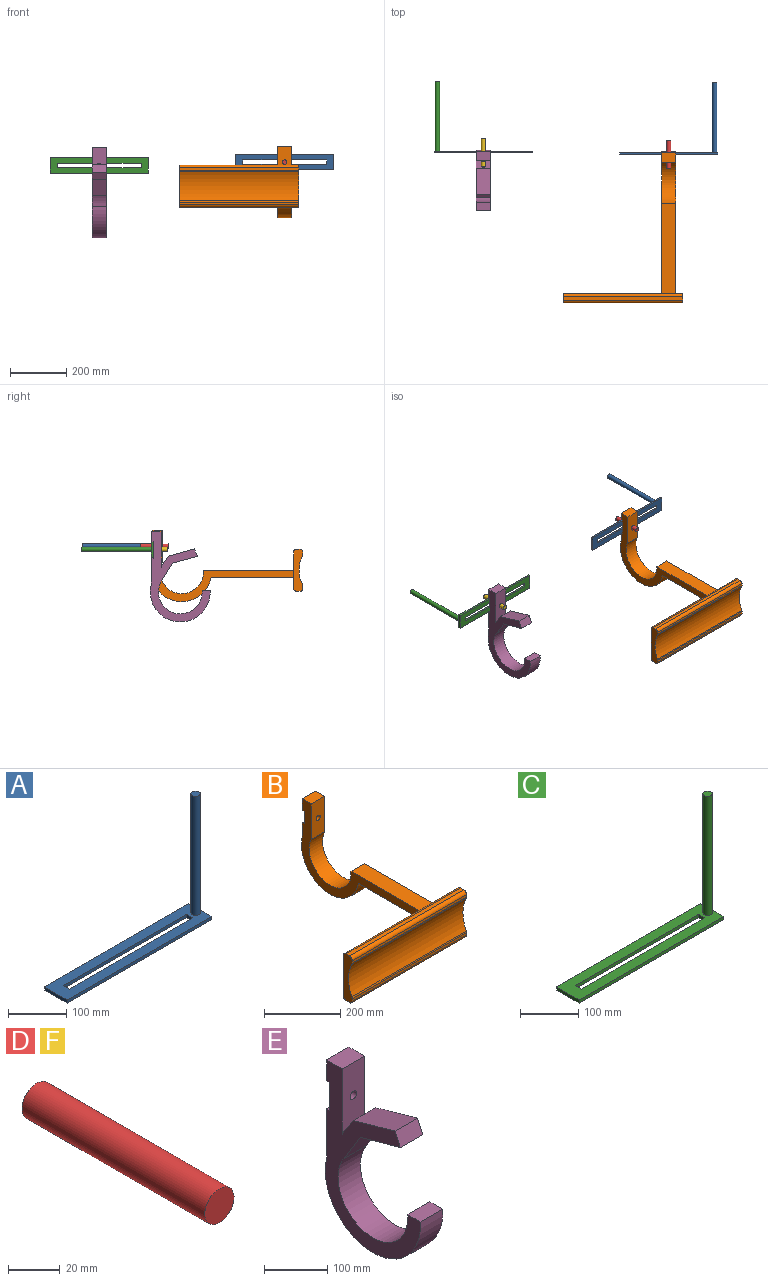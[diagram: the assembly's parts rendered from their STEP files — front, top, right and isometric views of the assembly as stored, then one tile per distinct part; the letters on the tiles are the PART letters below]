
ASSEMBLY  parts=6 mates=4
PART A: 12 faces, bbox 350x54.6x256.5 mm
  f0: plane 350x54.58mm, normal (0,0,1), area 14418.2mm2, adj f1,f3,f4,f5,f6,f7,f8,f9
  f1: plane 350x6.45mm, normal (0,-1,0), area 2257.7mm2, adj f0,f2,f4,f5
  f2: plane 350x54.58mm, normal (0,0,-1), area 14619.2mm2, adj f1,f3,f4,f5,f6,f7,f8,f9
  f3: plane 350x6.45mm, normal (0,1,0), area 2257.7mm2, adj f0,f2,f4,f5
  f4: plane 54.58x6.45mm, normal (1,0,0), area 352.1mm2, adj f0,f1,f2,f3
  f5: plane 54.58x6.45mm, normal (-1,0,0), area 352.1mm2, adj f0,f1,f2,f3
  f6: plane 15x6.45mm, normal (1,0,0), area 96.8mm2, adj f0,f2,f7,f9
  f7: plane 298.97x6.45mm, normal (0,1,0), area 1928.6mm2, adj f0,f2,f6,f8
  f8: plane 15x6.45mm, normal (-1,0,0), area 96.8mm2, adj f0,f2,f7,f9
  f9: plane 298.97x6.45mm, normal (0,-1,0), area 1928.6mm2, adj f0,f2,f6,f8
  f10: cylinder r=8mm len=250mm, axis (0,0,-1), area 12566.4mm2, adj f0,f11
  f11: plane 16x16mm, normal (0,0,1), area 201.1mm2, adj f10
PART B: 31 faces, bbox 425x538.8x255.6 mm
  f0: plane 50x41.78mm, normal (0,1,0), area 2089.1mm2, adj f1,f2,f7,f29
  f1: plane 505.7x255.65mm, normal (-1,0,0), area 20440.9mm2, adj f0,f5,f6,f7,f8,f9,f10,f11
  f2: plane 505.7x255.65mm, normal (1,0,0), area 20440.9mm2, adj f0,f5,f6,f7,f8,f9,f10,f11
  f3: cylinder r=7.5mm len=27.51mm, axis (0,-1,0), area 1296.5mm2, adj f26,f30
  f4: plane 425x7.79mm, normal (0,-1,0), area 3309mm2, adj f13,f16,f19,f22
  f5: plane 294.09x50mm, normal (0,0,-1), area 14704.4mm2, adj f1,f2,f7,f11
  f6: plane 321.33x50mm, normal (0,0,1), area 16066.6mm2, adj f1,f2,f9,f11
  f7: cylinder r=106.68mm len=211.61mm, axis (-1,0,0), area 17291.3mm2, adj f0,f1,f2,f5
  f8: cylinder r=77.9mm len=155.59mm, axis (-1,0,0), area 13733.1mm2, adj f1,f2,f9,f10
  f9: plane 50x11.5mm, normal (0,1,0), area 574.8mm2, adj f1,f2,f6,f8
  f10: plane 50x0.16mm, normal (0,-0.55,0.83), area 9.4mm2, adj f1,f2,f8,f25
  f11: plane 425x130mm, normal (0,1,0), area 54000mm2, adj f1,f2,f5,f6,f13,f16,f21,f23
  f12: plane 425x7.79mm, normal (0,-1,0), area 3309mm2, adj f13,f16,f18,f20
  f13: plane 150x33.08mm, normal (-1,0,0), area 3853.4mm2, adj f4,f11,f12,f14,f15,f17,f18,f19
  f14: plane 425x13.08mm, normal (0,0,1), area 5558.4mm2, adj f13,f16,f22,f23
  f15: plane 425x13.08mm, normal (0,0,-1), area 5558.4mm2, adj f13,f16,f20,f21
  f16: plane 150x33.08mm, normal (1,0,0), area 3853.4mm2, adj f4,f11,f12,f14,f15,f17,f18,f19
  f17: cylinder r=115.34mm len=425mm, axis (1,0,0), area 46473mm2, adj f13,f16,f18,f19
  f18: cylinder r=10mm len=425mm, axis (1,0,0), area 2014.7mm2, adj f12,f13,f16,f17
  f19: cylinder r=10mm len=425mm, axis (1,0,0), area 2014.7mm2, adj f4,f13,f16,f17
  f20: cylinder r=10mm len=425mm, axis (-1,0,0), area 6675.9mm2, adj f12,f13,f15,f16
  f21: cylinder r=10mm len=425mm, axis (1,0,0), area 6675.9mm2, adj f11,f13,f15,f16
  f22: cylinder r=10mm len=425mm, axis (1,0,0), area 6675.9mm2, adj f4,f13,f14,f16
  f23: cylinder r=10mm len=425mm, axis (-1,0,0), area 6675.9mm2, adj f11,f13,f14,f16
  f24: plane 50x36.99mm, normal (0,1,0), area 1849.4mm2, adj f1,f2,f27,f28
  f25: plane 50x0.97mm, normal (0,-0.18,-0.98), area 49.5mm2, adj f1,f2,f10,f26
  f26: plane 114.23x50mm, normal (0,-1,0), area 5534.9mm2, adj f1,f2,f3,f25,f27
  f27: plane 50x33.43mm, normal (0,0,1), area 1671.5mm2, adj f1,f2,f24,f26
  f28: plane 50x5.92mm, normal (0,0,-1), area 295.9mm2, adj f1,f2,f24,f30
  f29: plane 50x5.92mm, normal (0,0,1), area 295.9mm2, adj f0,f1,f2,f30
  f30: plane 50x40.56mm, normal (0,1,0), area 1851.3mm2, adj f1,f2,f3,f28,f29
PART C: 12 faces, bbox 350x54.6x256.5 mm
  f0: plane 350x54.58mm, normal (0,0,1), area 14418.2mm2, adj f1,f3,f4,f5,f6,f7,f8,f9
  f1: plane 350x6.45mm, normal (0,-1,0), area 2257.7mm2, adj f0,f2,f4,f5
  f2: plane 350x54.58mm, normal (0,0,-1), area 14619.2mm2, adj f1,f3,f4,f5,f6,f7,f8,f9
  f3: plane 350x6.45mm, normal (0,1,0), area 2257.7mm2, adj f0,f2,f4,f5
  f4: plane 54.58x6.45mm, normal (1,0,0), area 352.1mm2, adj f0,f1,f2,f3
  f5: plane 54.58x6.45mm, normal (-1,0,0), area 352.1mm2, adj f0,f1,f2,f3
  f6: plane 15x6.45mm, normal (1,0,0), area 96.8mm2, adj f0,f2,f7,f9
  f7: plane 298.97x6.45mm, normal (0,1,0), area 1928.6mm2, adj f0,f2,f6,f8
  f8: plane 15x6.45mm, normal (-1,0,0), area 96.8mm2, adj f0,f2,f7,f9
  f9: plane 298.97x6.45mm, normal (0,-1,0), area 1928.6mm2, adj f0,f2,f6,f8
  f10: cylinder r=8mm len=250mm, axis (0,0,-1), area 12566.4mm2, adj f0,f11
  f11: plane 16x16mm, normal (0,0,1), area 201.1mm2, adj f10
PART D: 3 faces, bbox 16x100x16 mm
  f0: cylinder r=8mm len=100mm, axis (0,1,0), area 5026.5mm2, adj f1,f2
  f1: plane 16x16mm, normal (0,-1,0), area 201.1mm2, adj f0
  f2: plane 16x16mm, normal (0,1,0), area 201.1mm2, adj f0
PART E: 18 faces, bbox 50x213.4x321.8 mm
  f0: plane 50x38.58mm, normal (0,0.83,0.55), area 2311.2mm2, adj f5,f8,f9,f10
  f1: cylinder r=77.9mm len=155.8mm, axis (1,0,0), area 14842.3mm2, adj f2,f7,f8,f9
  f2: plane 59.19x50mm, normal (0,-0.85,-0.52), area 3468.9mm2, adj f1,f3,f8,f9
  f3: plane 89.74x50mm, normal (0,-0.27,-0.96), area 4653.8mm2, adj f2,f4,f8,f9
  f4: plane 50x26.48mm, normal (0,-0.92,0.39), area 1440mm2, adj f3,f5,f8,f9
  f5: plane 93.22x50mm, normal (0,0.27,0.96), area 4845.3mm2, adj f0,f4,f8,f9
  f6: cylinder r=106.68mm len=213.37mm, axis (1,0,0), area 18299.7mm2, adj f7,f8,f9,f16
  f7: plane 50x28.84mm, normal (0,0,1), area 1442mm2, adj f1,f6,f8,f9
  f8: plane 321.77x213.37mm, normal (-1,0,0), area 19860.3mm2, adj f0,f1,f2,f3,f4,f5,f6,f7
  f9: plane 321.77x213.37mm, normal (1,0,0), area 19860.3mm2, adj f0,f1,f2,f3,f4,f5,f6,f7
  f10: plane 126.11x50mm, normal (0,-1,0), area 6128.8mm2, adj f0,f8,f9,f11,f17
  f11: plane 50x35.17mm, normal (0,0,1), area 1758.4mm2, adj f8,f9,f10,f12
  f12: plane 50x40.08mm, normal (0,1,0), area 2004.2mm2, adj f8,f9,f11,f13
  f13: plane 50x6.45mm, normal (0,0,-1), area 322.5mm2, adj f8,f9,f12,f14
  f14: plane 54.58x50mm, normal (0,1,0), area 2552.3mm2, adj f8,f9,f13,f15,f17
  f15: plane 50x6.45mm, normal (0,0,1), area 322.5mm2, adj f8,f9,f14,f16
  f16: plane 95.56x50mm, normal (0,1,0), area 4778mm2, adj f6,f8,f9,f15
  f17: cylinder r=7.5mm len=28.72mm, axis (0,-1,0), area 1353.3mm2, adj f10,f14
PART F: same geometry as D
PLACE A rot(axis=(-1,0,0),90deg) t=(-449.63,46.88,-48.83)mm
PLACE B t=(-499.63,-140.4,-1552.51)mm
PLACE C rot(axis=(0,0.71,0.71),180deg) t=(-585.03,349.76,-33.67)mm
PLACE D rot(axis=(1,0,0),0deg) t=(-234.28,92.5,-60.33)mm
PLACE E t=(-701.03,-135.25,-1624.66)mm
PLACE F t=(-895.68,98.38,-72.3)mm
MATE fastened A.f2 <-> D.f0  axis (0,-1,0) through (-274.63,42.5,-35.27)mm
MATE fastened F.f0 <-> E.f17  axis (0,1,0) through (-936.03,48.38,-47.24)mm
MATE fastened D.f0 <-> B.f3  axis (0,1,0) through (-274.63,42.5,-35.27)mm
MATE fastened C.f2 <-> F.f0  axis (0,-1,0) through (-936.03,48.38,-47.24)mm
